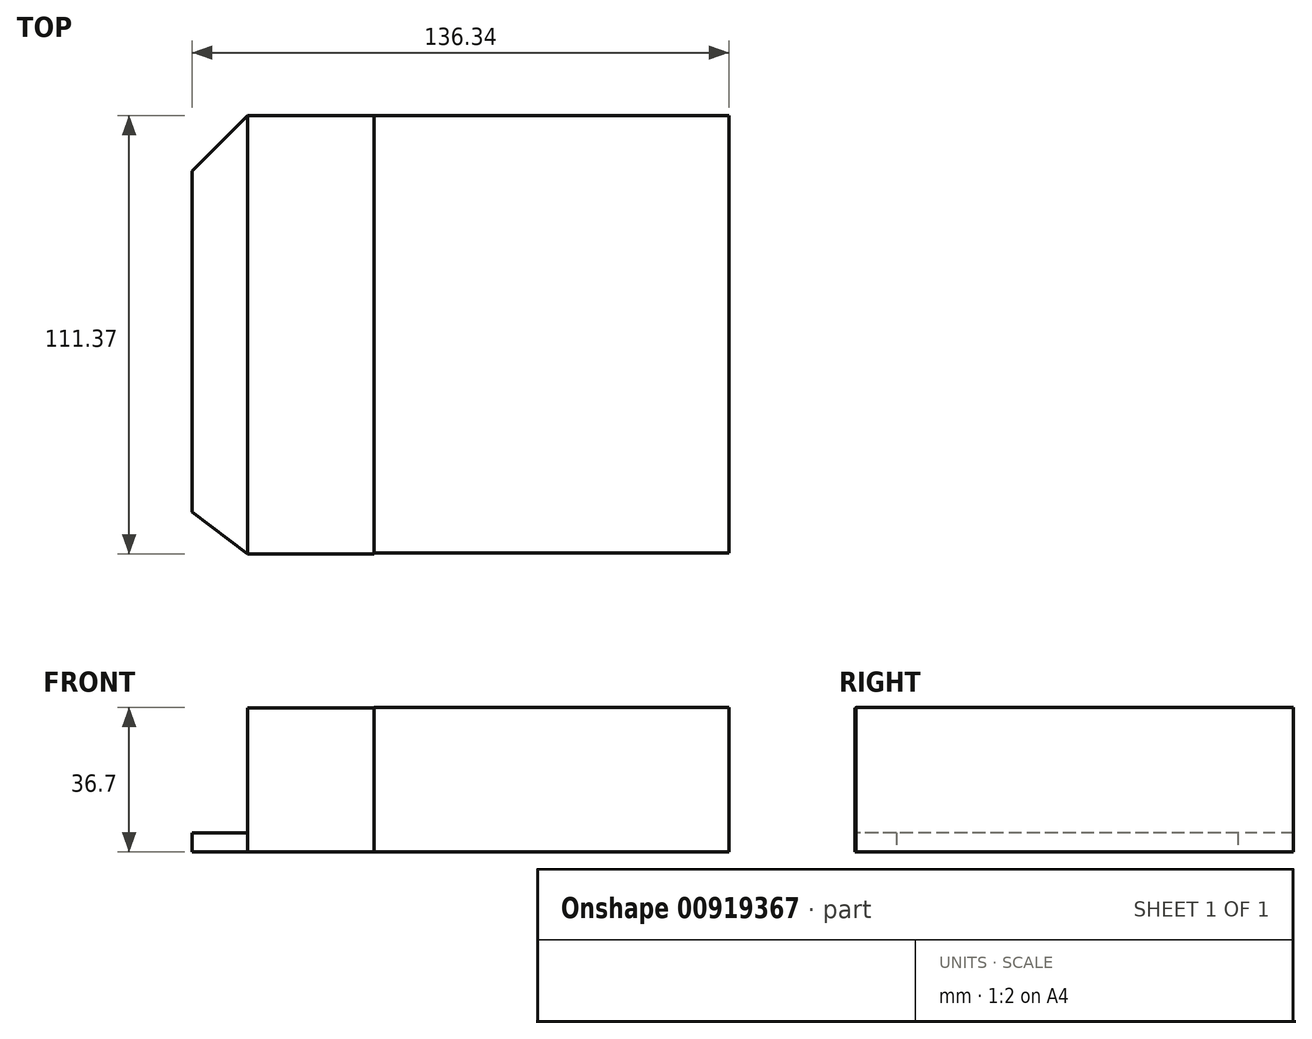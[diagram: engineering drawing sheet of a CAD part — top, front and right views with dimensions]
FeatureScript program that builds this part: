
annotation { "Feature Type Name" : "Feature", "Feature Type Description" : "" }
export const myFeature = defineFeature(function(context is Context, id is Id, definition is map)
    precondition{}
    {
        {
            var Q0;
            Q0=qCreatedBy(makeId("Top.planeOp"),FACE);
            var sketch = newSketch(context, id + "F0", { "sketchPlane" : qUnion([Q0])});
            skLineSegment(sketch, "E0.bottom", {"start": v(-42.89, 52.3) * mm, "end": v(47.32, 52.3) * mm});
            skLineSegment(sketch, "E0.top", {"start": v(-42.89, -58.76) * mm, "end": v(47.32, -58.76) * mm});
            skLineSegment(sketch, "E0.left", {"start": v(-42.89, 52.3) * mm, "end": v(-42.89, -58.76) * mm});
            skLineSegment(sketch, "E0.right", {"start": v(47.32, 52.3) * mm, "end": v(47.32, -58.76) * mm});
            skLineSegment(sketch, "E1.bottom", {"start": v(-42.89, 52.3) * mm, "end": v(-74.97, 52.3) * mm});
            skLineSegment(sketch, "E1.top", {"start": v(-42.89, -59.06) * mm, "end": v(-74.97, -59.06) * mm});
            skLineSegment(sketch, "E1.left", {"start": v(-42.89, 52.3) * mm, "end": v(-42.89, -59.06) * mm});
            skLineSegment(sketch, "E1.right", {"start": v(-74.97, 52.3) * mm, "end": v(-74.97, -59.06) * mm});
            skLineSegment(sketch, "E2", {"start": v(-74.97, 52.3) * mm, "end": v(-89.02, 38.25) * mm});
            skLineSegment(sketch, "E3", {"start": v(-89.02, 38.25) * mm, "end": v(-89.02, -48.46) * mm});
            skLineSegment(sketch, "E4", {"start": v(-89.02, -48.46) * mm, "end": v(-74.97, -59.06) * mm});
            skSolve(sketch);
        }
        {
            var Q0;
            {var subQ0=sQuery(id+"F0.wireOp",EDGE,"E0.bottom");Q0=makeQuery(id+"F0.imprint","IMPRINT",FACE,{"disambiguationData":[TD([[makeQuery(id+"F0.imprint","IMPRINT",EDGE,{"derivedFrom":subQ0}),-1.0]])]});}
            extrude(context, id + "F1", {"entities" : qUnion([Q0]), "depth" : 36.7 * mm, "offsetDistance" : 25 * mm});
        }
        {
            var Q0;
            {var subQ3=sQuery(id+"F0.wireOp",EDGE,"E1.bottom");Q0=makeQuery(id+"F0.imprint","IMPRINT",FACE,{"disambiguationData":[TD([[makeQuery(id+"F0.imprint","IMPRINT",EDGE,{"derivedFrom":subQ3}),1.0]])]});}
            extrude(context, id + "F2", {"entities" : qUnion([Q0]), "depth" : 36.6 * mm, "offsetDistance" : 25 * mm});
        }
        {
            var Q0;
            Q0=makeQuery(id+"F0.imprint","IMPRINT",FACE,{"disambiguationData":[TD([[makeQuery(id+"F0.imprint","IMPRINT",EDGE,{"derivedFrom":sQuery(id+"F0.wireOp",EDGE,"E1.right")}),-1.0]])]});
            extrude(context, id + "F3", {"entities" : qUnion([Q0]), "depth" : 4.8 * mm, "offsetDistance" : 25 * mm});
        }
    });
